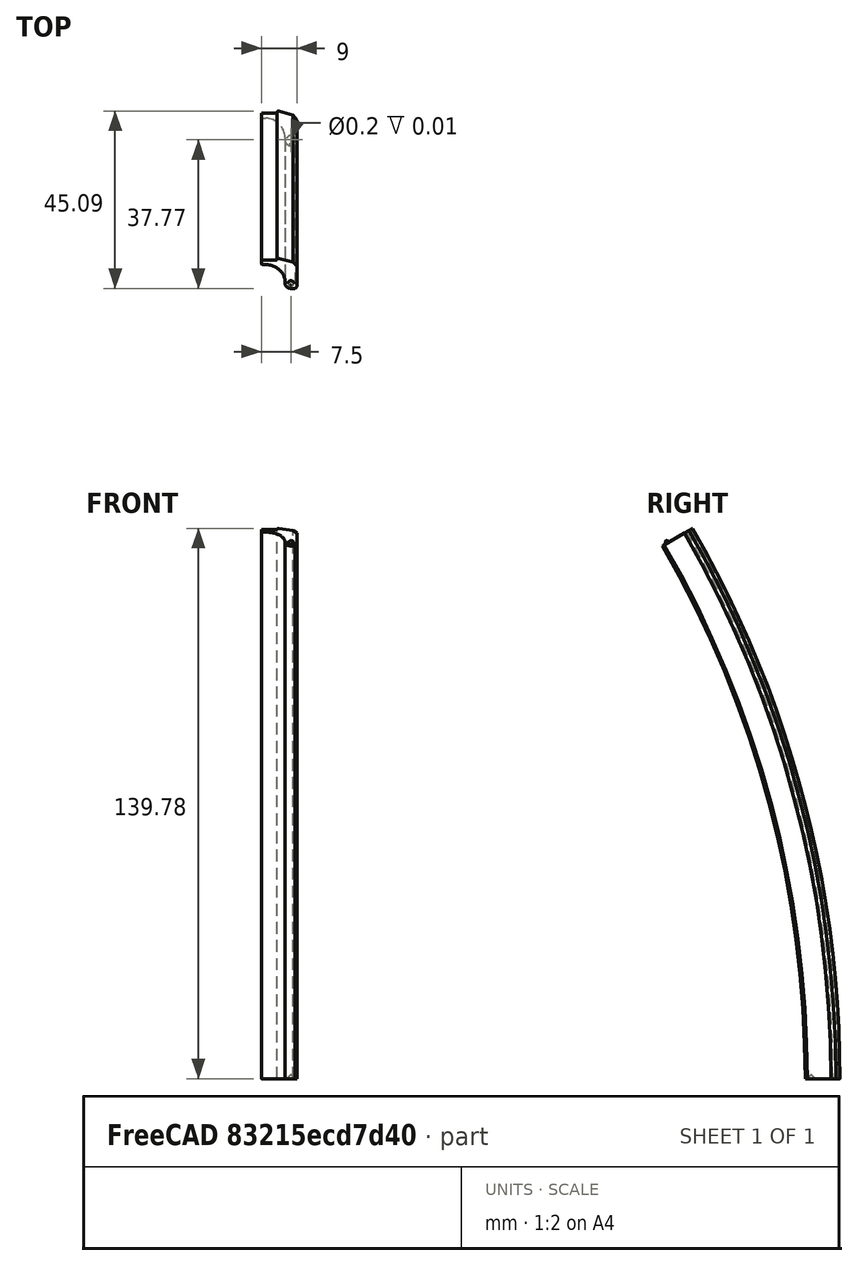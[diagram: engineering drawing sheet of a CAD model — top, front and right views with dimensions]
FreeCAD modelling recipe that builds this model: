
FCSTD DOCUMENT  (FreeCAD 0.16R)
Label: 1e2spacer
License: All rights reserved
LicenseURL: http://en.wikipedia.org/wiki/All_rights_reserved
objects: PartDesign::Fillet×4, PartDesign::Chamfer×4, Sketcher::SketchObject×3, PartDesign::Revolution×1, PartDesign::Pad×1, PartDesign::Pocket×1, Mesh::Feature×1
note: 17 computed .brp shape members not serialized (recipe doc carries the construction recipe); baked Part::Feature solids carry a one-line shape summary decoded from their .brp

FEATURE [Sketcher::SketchObject] Sketch
  sketch-geometry (8):
    g0: LineSegment StartX=0 StartY=279 StartZ=0 EndX=4 EndY=279 EndZ=0
    g1: LineSegment StartX=4 StartY=279 StartZ=0 EndX=4 EndY=279.7 EndZ=0
    g2: LineSegment StartX=0 StartY=277.75 StartZ=0 EndX=0 EndY=279 EndZ=0
    g3: LineSegment StartX=0 StartY=277.75 StartZ=0 EndX=6 EndY=277.75 EndZ=0
    g4: LineSegment StartX=6 StartY=277.75 StartZ=0 EndX=6 EndY=270.75 EndZ=0
    g5: LineSegment StartX=6 StartY=270.75 StartZ=0 EndX=9 EndY=270.75 EndZ=0
    g6: LineSegment StartX=9 StartY=270.75 StartZ=0 EndX=9 EndY=278.25 EndZ=0
    g7: LineSegment StartX=4 StartY=279.7 StartZ=0 EndX=9 EndY=278.25 EndZ=0
  constraints (24):
    c: Horizontal(g0)
    c: PointOnObject(g0,g-2)
    c: DistanceY(g0) = 279
    c: Distance(g0) = 4
    c: Coincident(g1,g0)
    c: Vertical(g1)
    c: Distance(g1) = 0.7
    c: Vertical(g2)
    c: Coincident(g2,g0)
    c: Distance(g2) = 1.25
    c: Horizontal(g3)
    c: Coincident(g3,g2)
    c: Distance(g3) = 6
    c: Vertical(g4)
    c: Coincident(g4,g3)
    c: Distance(g4) = 7
    c: Horizontal(g5)
    c: Coincident(g5,g4)
    c: Distance(g5) = 3
    c: Vertical(g6)
    c: Coincident(g5,g6)
    c: Distance(g6) = 7.5
    c: Coincident(g7,g1)
    c: Coincident(g7,g6)
FEATURE [PartDesign::Revolution] Revolution
  Angle = 30
  Axis = (1,0,0)
  Base = (0,0,0)
  ReferenceAxis = -> Sketch [H_Axis]
  Sketch = -> Sketch
FEATURE [PartDesign::Fillet] Fillet
  Base = -> Revolution [Edge17]
  Radius = 5
FEATURE [PartDesign::Fillet] Fillet001
  Base = -> Fillet [Edge26]
  Radius = 0.4
FEATURE [PartDesign::Fillet] Fillet002
  Base = -> Fillet001 [Edge20]
  Radius = 1.5
FEATURE [PartDesign::Fillet] Fillet003
  Base = -> Fillet002 [Edge27]
  Radius = 0.3
FEATURE [PartDesign::Chamfer] Chamfer
  Base = -> Fillet003 [Edge30]
  Size = 0.5
FEATURE [PartDesign::Chamfer] Chamfer001
  Base = -> Chamfer [Edge21]
  Size = 1
FEATURE [Sketcher::SketchObject] Sketch001
  ExternalGeometry = -> [Chamfer001]
  Placement = pos=(0,0,0) rot=(1,0,0;0.523599rad)
  Support = -> Chamfer001 [Face16]
  sketch-geometry (1):
    g0: Circle CenterX=7.5 CenterY=272.25 CenterZ=0 NormalX=0 NormalY=0 NormalZ=1 Radius=0.75
  constraints (3):
    c: Radius(g0) = 0.75
    c: Distance(g0,g-3) = 1.5
    c: Distance(g0,g-4) = 1.5
FEATURE [PartDesign::Pad] Pad
  Length = 0.75
  Length2 = 100
  Sketch = -> Sketch001
  Type = 0
FEATURE [PartDesign::Chamfer] Chamfer002
  Base = -> Pad [Edge1]
  Size = 0.72
FEATURE [Sketcher::SketchObject] Sketch002
  ExternalGeometry = -> [Chamfer002]
  Placement = pos=(0,0,0) rot=(1,0,0;3.14159rad)
  Support = -> Chamfer002 [Face19]
  sketch-geometry (1):
    g0: Circle CenterX=7.5 CenterY=-272.25 CenterZ=0 NormalX=0 NormalY=0 NormalZ=1 Radius=0.1
  constraints (3):
    c: Distance(g0,g-4) = 1.5
    c: Distance(g0,g-3) = 1.5
    c: Radius(g0) = 0.1
FEATURE [PartDesign::Pocket] Pocket
  Length = 1
  Sketch = -> Sketch002
  Type = 0
FEATURE [PartDesign::Chamfer] Chamfer003
  Base = -> Pocket [Edge48]
  Size = 0.99
FEATURE [Mesh::Feature] Mesh  label="Chamfer003 (Meshed)"
